# Revit family: Скамейка чугунная «Новая Европа» Арт 7220
name_source: partatom
category: Антураж
revit_build: Autodesk Revit 2018 (Build: 20180423_1000(x64)
units: mm (PartAtom-declared; Revit-internal decimal feet)

## family parameters
Всегда вертикально = Да
Источник визуального образа = Геометрия семейства
На основе рабочей плоскости = Нет
Общий = Нет
При загрузке вырезать с полостями = Нет
Точка расчета площади = Нет

## types (6) — shared parameters
URL = https://hobbyka.ru
Артикул товара = Арт. 7220
Высота = 725 мм
Группа модели = Садовые скамейки
Изготовитель = ООО «Хоббика»
Изображение типоразмера = Скамейка чугунная «Новая Европа» Арт 7220.jpg
Материал изделия = Чугун, дерево
Цвет лавки = Дерево
Цвет опор = Чугун
Ширина = 685 мм

## per-type parameters (varying)
| type | Версия 0,6 м (кресло) | Версия 1,5 м | Версия 1,8 м | Версия 2,0 м | Версия 2,0 м (3 опоры) | Версия 3,0 м (3 опоры) | Длина | Описание | Средняя опора |
| Версия 0,6 м (кресло) | Да | Нет | Нет | Нет | Нет | Нет | 600 мм | Скамейка чугунная «Новая Европа». Версия 0,6 м Кресло | Нет |
| Версия 1,5 м | Нет | Да | Нет | Нет | Нет | Нет | 1500 мм | Скамейка чугунная «Новая Европа». Версия 1,5 м | Нет |
| Версия 1,8 м | Нет | Нет | Да | Нет | Нет | Нет | 1800 мм | Скамейка чугунная «Новая Европа». Версия 1,8 м | Нет |
| Версия 2,0 м | Нет | Нет | Нет | Да | Нет | Нет | 2000 мм | Скамейка чугунная «Новая Европа». Версия 2,0 м | Нет |
| Версия 2,0 м (3 опоры) | Нет | Нет | Нет | Нет | Да | Нет | 2000 мм | Скамейка чугунная «Новая Европа». Версия 2,0 м (3 опоры) | Да |
| Версия 3,0 м (3 опоры) | Нет | Нет | Нет | Нет | Нет | Да | 3000 мм | Скамейка чугунная «Новая Европа». Версия 3,0 м (3 опоры) | Да |
